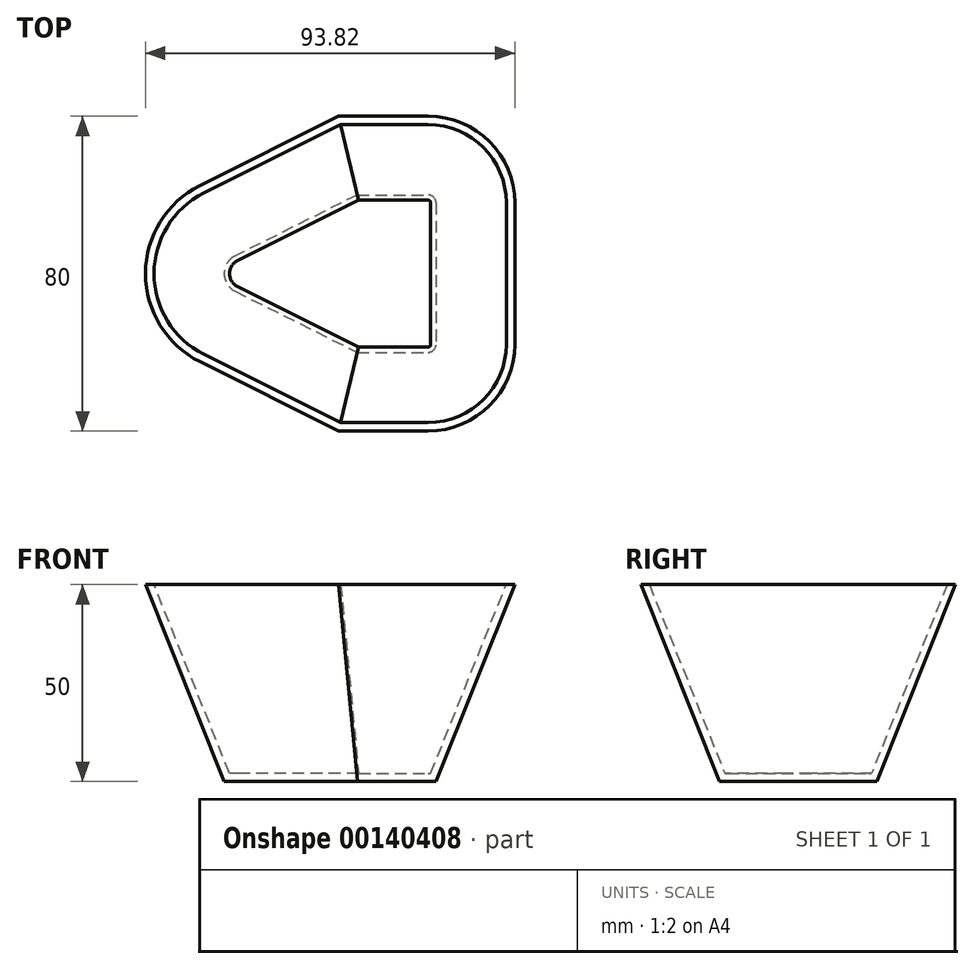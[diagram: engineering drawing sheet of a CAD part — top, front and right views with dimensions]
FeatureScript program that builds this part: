
annotation { "Feature Type Name" : "Feature", "Feature Type Description" : "" }
export const myFeature = defineFeature(function(context is Context, id is Id, definition is map)
    precondition{}
    {
        {
            var Q0;
            Q0=qCreatedBy(makeId("Top.planeOp"),FACE);
            var sketch = newSketch(context, id + "F0", { "sketchPlane" : qUnion([Q0])});
            skLineSegment(sketch, "E0.bottom", {"start": v(-50.46, 20) * mm, "end": v(-32.46, 20) * mm});
            skLineSegment(sketch, "E0.top", {"start": v(-50.46, -20) * mm, "end": v(-32.46, -20) * mm});
            skLineSegment(sketch, "E0.left", {"start": v(-50.46, 20) * mm, "end": v(-50.46, -20) * mm, "construction": true});
            skLineSegment(sketch, "E0.right", {"start": v(-30.46, 18) * mm, "end": v(-30.46, -18) * mm});
            skLineSegment(sketch, "E1", {"start": v(-50.46, 20) * mm, "end": v(-81.52, 4.47) * mm});
            skLineSegment(sketch, "E2", {"start": v(-81.52, -4.47) * mm, "end": v(-50.46, -20) * mm});
            skPoint(sketch, "E3.visualSharp", {"position": v(-90.46, 0) * mm});
            skArc(sketch, "E3.filletArc", {"start": v(-81.52, 4.47) * mm, "mid": v(-84.28, 0) * mm, "end": v(-81.52, -4.47) * mm});
            skPoint(sketch, "E4.visualSharp", {"position": v(-30.46, 20) * mm});
            skArc(sketch, "E4.filletArc", {"start": v(-30.46, 18) * mm, "mid": v(-31.05, 19.41) * mm, "end": v(-32.46, 20) * mm});
            skPoint(sketch, "E5.visualSharp", {"position": v(-30.46, -20) * mm});
            skArc(sketch, "E5.filletArc", {"start": v(-32.46, -20) * mm, "mid": v(-31.05, -19.41) * mm, "end": v(-30.46, -18) * mm});
            skSolve(sketch);
        }
        {
            var Q0;
            Q0=makeQuery(id+"F0.imprint","IMPRINT",FACE,{"disambiguationData":[TD([[makeQuery(id+"F0.imprint","IMPRINT",EDGE,{"derivedFrom":sQuery(id+"F0.wireOp",EDGE,"E0.bottom")}),-1.0]])]});
            cPlane(context, id + "F1", {"entities" : qUnion([Q0]), "cplaneType" : CPlaneType.OFFSET, "offset" : 50 * mm, "width" : 150 * mm, "height" : 150 * mm});
        }
        {
            var Q0;
            Q0=qCreatedBy(id+"F1.planeOp",FACE);
            var sketch = newSketch(context, id + "F2", { "sketchPlane" : qUnion([Q0])});
            skArc(sketch, "E6.0", {"start": v(-10.46, 18) * mm, "mid": v(-16.9, 33.56) * mm, "end": v(-32.46, 40) * mm});
            skLineSegment(sketch, "E6.1", {"start": v(-10.46, -18) * mm, "end": v(-10.46, 18) * mm});
            skLineSegment(sketch, "E6.2", {"start": v(-32.46, 40) * mm, "end": v(-55.18, 40) * mm});
            skArc(sketch, "E6.3", {"start": v(-32.46, -40) * mm, "mid": v(-16.9, -33.56) * mm, "end": v(-10.46, -18) * mm});
            skLineSegment(sketch, "E6.4", {"start": v(-55.18, 40) * mm, "end": v(-90.46, 22.36) * mm});
            skArc(sketch, "E6.5", {"start": v(-90.46, 22.36) * mm, "mid": v(-104.28, 0) * mm, "end": v(-90.46, -22.36) * mm});
            skLineSegment(sketch, "E6.6", {"start": v(-90.46, -22.36) * mm, "end": v(-55.18, -40) * mm});
            skLineSegment(sketch, "E6.7", {"start": v(-55.18, -40) * mm, "end": v(-32.46, -40) * mm});
            skSolve(sketch);
        }
        {
            var Q0;
            Q0=makeQuery(id+"F2.imprint","IMPRINT",FACE,{"disambiguationData":[TD([[makeQuery(id+"F2.imprint","IMPRINT",EDGE,{"derivedFrom":sQuery(id+"F2.wireOp",EDGE,"E6.0")}),1.0]])]});
            var Q1;
            Q1=makeQuery(id+"F0.imprint","IMPRINT",FACE,{"disambiguationData":[TD([[makeQuery(id+"F0.imprint","IMPRINT",EDGE,{"derivedFrom":sQuery(id+"F0.wireOp",EDGE,"E0.bottom")}),-1.0]])]});
            loft(context, id + "F3", {"sheetProfilesArray" : [{ "sheetProfileEntities" : qUnion([Q0]) }, { "sheetProfileEntities" : qUnion([Q1]) }]});
        }
        {
            var Q0;
            Q0=makeQuery(id+"F3.opLoft","CAP_FACE",FACE,{"disambiguationData":[OSD([makeQuery(id+"F2.imprint","IMPRINT",FACE,{"disambiguationData":[TD([[makeQuery(id+"F2.imprint","IMPRINT",EDGE,{"derivedFrom":sQuery(id+"F2.wireOp",EDGE,"E6.0")}),1.0]])]})])],"isStart":true});
            shell(context, id + "F4", {"entities" : qUnion([Q0]), "thickness" : 2 * mm});
        }
    });
